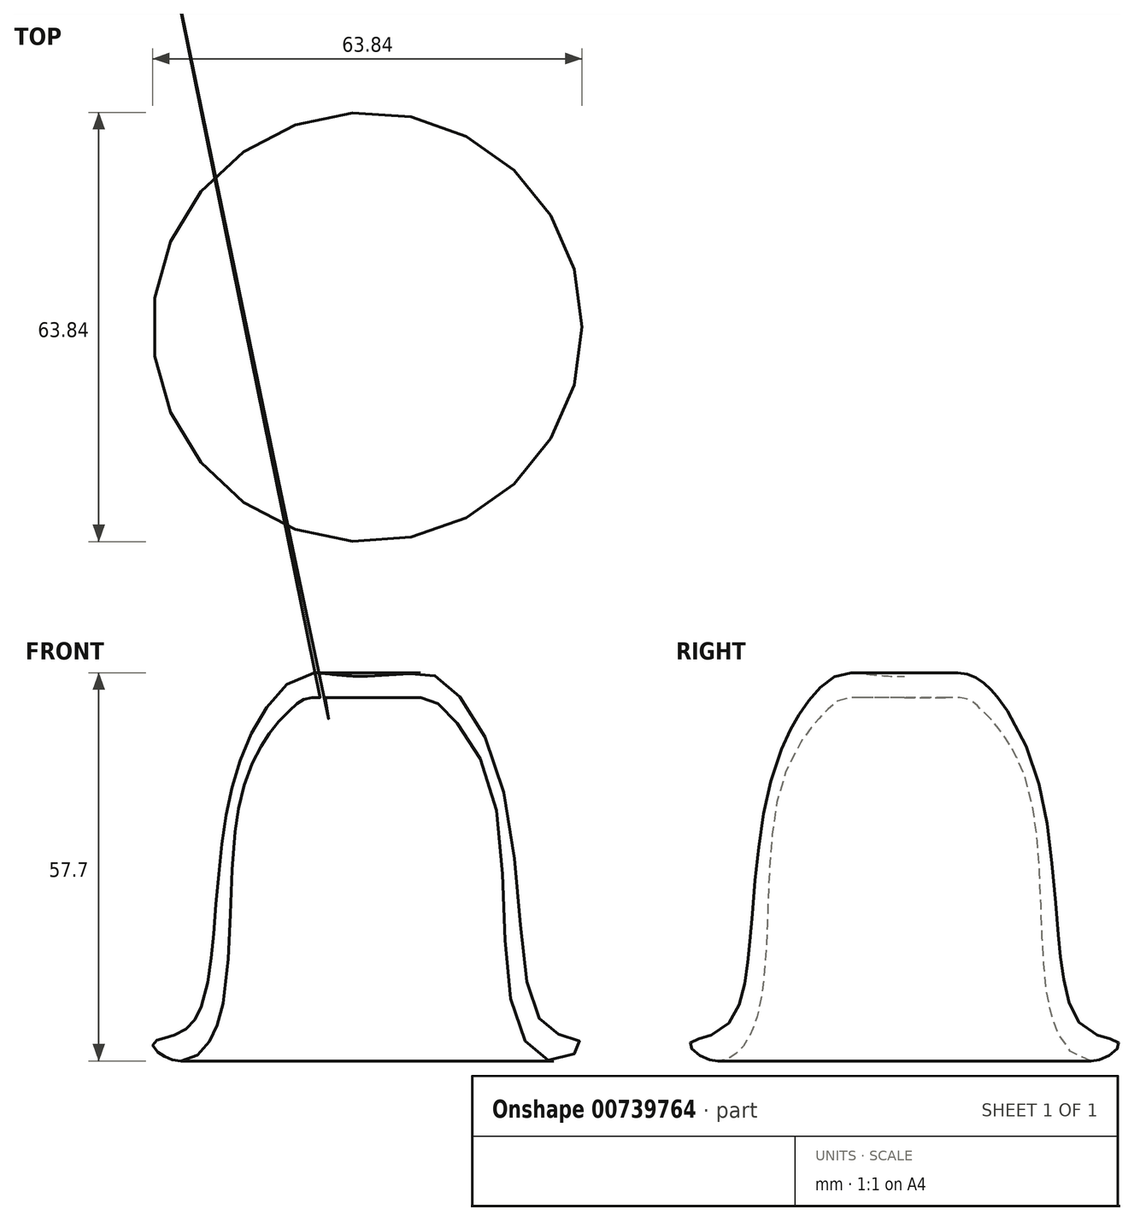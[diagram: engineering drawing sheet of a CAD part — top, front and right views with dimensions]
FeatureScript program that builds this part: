
annotation { "Feature Type Name" : "Feature", "Feature Type Description" : "" }
export const myFeature = defineFeature(function(context is Context, id is Id, definition is map)
    precondition{}
    {
        {
            var Q0;
            Q0=qCreatedBy(makeId("Front.planeOp"),FACE);
            var sketch = newSketch(context, id + "F0", { "sketchPlane" : qUnion([Q0])});
            skFitSpline(sketch, "E0", {"points": [v(0, 57.15) * mm, v(10.32, 57.15) * mm, v(20, 41.12) * mm, v(24.63, 8.16) * mm, v(29.16, 3.69) * mm, v(31.92, 2.45) * mm, v(28.01, 0) * mm, v(21.8, 6.95) * mm, v(18.24, 41.26) * mm, v(10.73, 52.88) * mm, v(0, 53.98) * mm], "startDerivative": vector(201.75, 0.28) * mm, "endDerivative": vector(-296.25, -1.74) * mm});
            skLineSegment(sketch, "E1", {"start": v(0, 57.15) * mm, "end": v(0, 53.98) * mm});
            skSolve(sketch);
        }
        {
            var Q0;
            Q0=qCreatedBy(makeId("Front.planeOp"),FACE);
            var sketch = newSketch(context, id + "F1", { "sketchPlane" : qUnion([Q0])});
            skLineSegment(sketch, "E2", {"start": v(0, 72.71) * mm, "end": v(0, -45.46) * mm});
            skSolve(sketch);
        }
        {
            var Q0;
            Q0=makeQuery(id+"F0.imprint","IMPRINT",FACE,{"disambiguationData":[TD([[makeQuery(id+"F0.imprint","IMPRINT",EDGE,{"derivedFrom":sQuery(id+"F0.wireOp",EDGE,"E0")}),-1.0]])]});
            var Q1;
            Q1=sQuery(id+"F1.wireOp",EDGE,"E2");
            revolve(context, id + "F2", {"surfaceOperationType" : NewSurfaceOperationType.NEW, "entities" : qUnion([Q0]), "axis" : qUnion([Q1]), "revolveType" : RevolveType.FULL});
        }
    });
